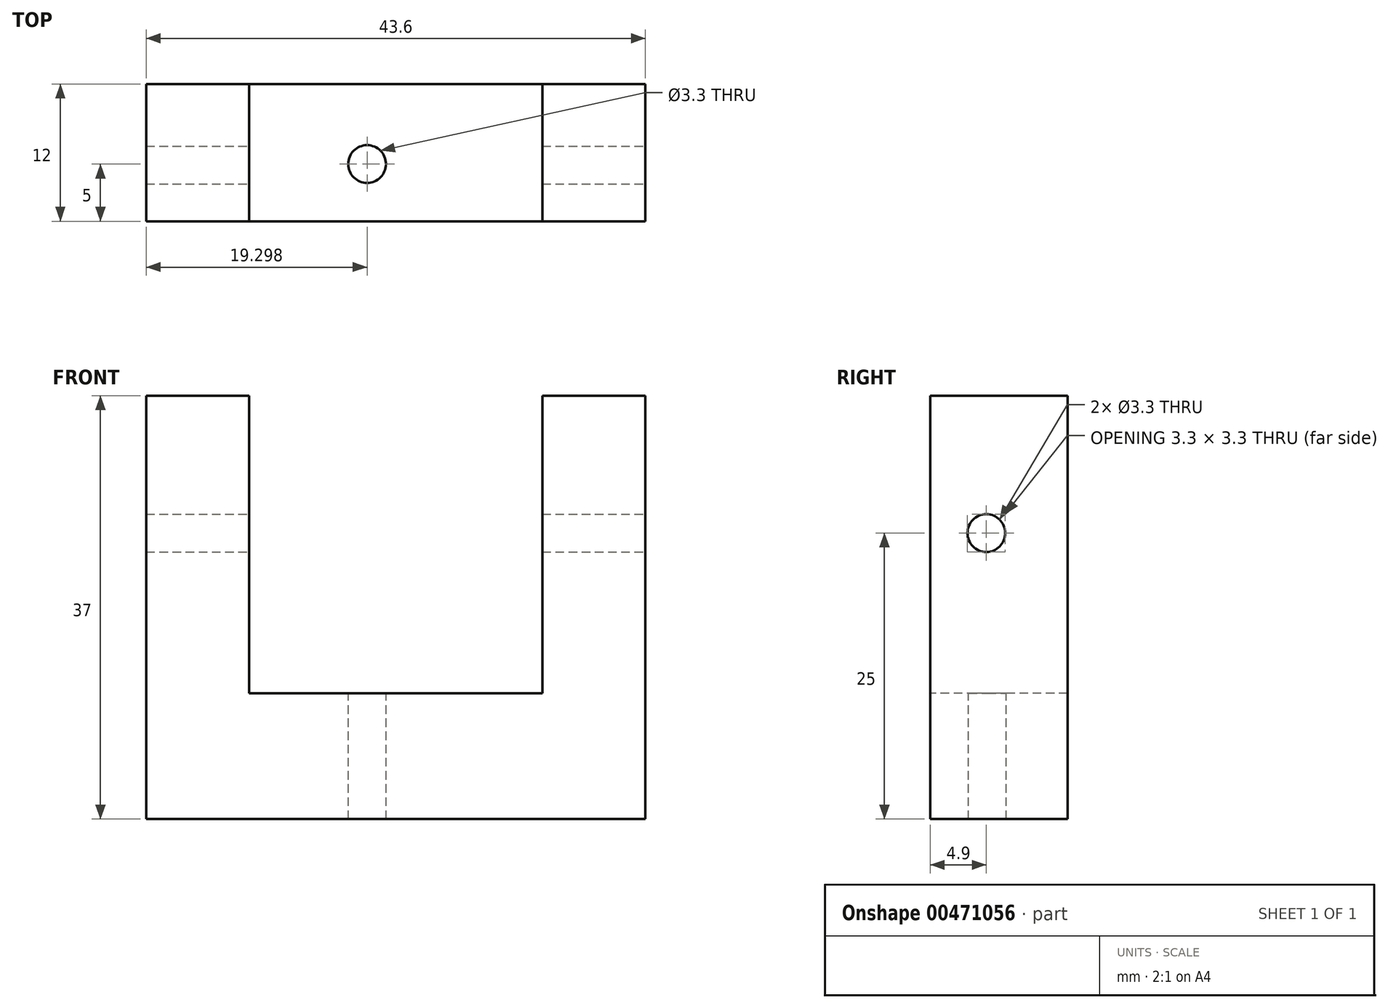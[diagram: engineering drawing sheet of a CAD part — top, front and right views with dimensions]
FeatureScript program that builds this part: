
annotation { "Feature Type Name" : "Feature", "Feature Type Description" : "" }
export const myFeature = defineFeature(function(context is Context, id is Id, definition is map)
    precondition{}
    {
        {
            var Q0;
            Q0=qCreatedBy(makeId("Front.planeOp"),FACE);
            var sketch = newSketch(context, id + "F0", { "sketchPlane" : qUnion([Q0])});
            skLineSegment(sketch, "E0", {"start": v(-83.52, 0) * mm, "end": v(-83.52, -37) * mm});
            skLineSegment(sketch, "E1", {"start": v(-83.52, -37) * mm, "end": v(-39.92, -37) * mm});
            skLineSegment(sketch, "E2", {"start": v(-39.92, -37) * mm, "end": v(-39.92, 0) * mm});
            skLineSegment(sketch, "E3", {"start": v(-39.92, 0) * mm, "end": v(-48.92, 0) * mm});
            skLineSegment(sketch, "E4", {"start": v(-48.92, 0) * mm, "end": v(-48.92, -26) * mm});
            skLineSegment(sketch, "E5", {"start": v(-48.92, -26) * mm, "end": v(-74.52, -26) * mm});
            skLineSegment(sketch, "E6", {"start": v(-74.52, -26) * mm, "end": v(-74.52, 0) * mm});
            skLineSegment(sketch, "E7", {"start": v(-74.52, 0) * mm, "end": v(-83.52, 0) * mm});
            skSolve(sketch);
        }
        {
            var Q0;
            Q0 = qSketchRegion(id + "F0", true);
            extrude(context, id + "F1", {"entities" : qUnion([Q0]), "oppositeDirection" : true, "depth" : 12 * mm, "offsetDistance" : 25 * mm});
        }
        {
            var Q0;
            Q0=qCreatedBy(makeId("Right.planeOp"),FACE);
            var sketch = newSketch(context, id + "F2", { "sketchPlane" : qUnion([Q0])});
            skCircle(sketch, "E8", {"center": v(4.9, -12) * mm, "radius": 1.65 * mm});
            skSolve(sketch);
        }
        {
            var Q0;
            Q0=qCreatedBy(makeId("Top.planeOp"),FACE);
            var sketch = newSketch(context, id + "F3", { "sketchPlane" : qUnion([Q0])});
            skCircle(sketch, "E9", {"center": v(-64.22, 5) * mm, "radius": 1.65 * mm});
            skSolve(sketch);
        }
        {
            var Q0;
            Q0=sQuery(id+"F3.wireOp",VERTEX,"E9.center");
            var Q1;
            Q1=makeQuery(id+"F1.opExtrude","SWEPT_BODY",BODY,{"disambiguationData":[OSD([sQuery(id+"F0.wireOp",EDGE,"E0"),sQuery(id+"F0.wireOp",EDGE,"E1"),sQuery(id+"F0.wireOp",EDGE,"E2"),sQuery(id+"F0.wireOp",EDGE,"E3"),sQuery(id+"F0.wireOp",EDGE,"E4"),sQuery(id+"F0.wireOp",EDGE,"E5"),sQuery(id+"F0.wireOp",EDGE,"E6"),sQuery(id+"F0.wireOp",EDGE,"E7")])]});
            hole(context, id + "F4", {"style" : HoleStyle.SIMPLE, "endStyle" : HoleEndStyle.THROUGH, "holeDiameter" : 3.3 * mm, "isTappedThrough" : true, "tappedDepth" : 12 * mm, "tapClearance" : 3, "locations" : qUnion([Q0]), "scope" : qUnion([Q1])});
        }
        {
            var Q0;
            Q0=sQuery(id+"F2.wireOp",VERTEX,"E8.center");
            var Q1;
            Q1=makeQuery(id+"F1.opExtrude","SWEPT_BODY",BODY,{"disambiguationData":[OSD([sQuery(id+"F0.wireOp",EDGE,"E0"),sQuery(id+"F0.wireOp",EDGE,"E1"),sQuery(id+"F0.wireOp",EDGE,"E2"),sQuery(id+"F0.wireOp",EDGE,"E3"),sQuery(id+"F0.wireOp",EDGE,"E4"),sQuery(id+"F0.wireOp",EDGE,"E5"),sQuery(id+"F0.wireOp",EDGE,"E6"),sQuery(id+"F0.wireOp",EDGE,"E7")])]});
            hole(context, id + "F5", {"style" : HoleStyle.SIMPLE, "endStyle" : HoleEndStyle.THROUGH, "holeDiameter" : 3.3 * mm, "isTappedThrough" : true, "tappedDepth" : 12 * mm, "tapClearance" : 3, "locations" : qUnion([Q0]), "scope" : qUnion([Q1])});
        }
    });
